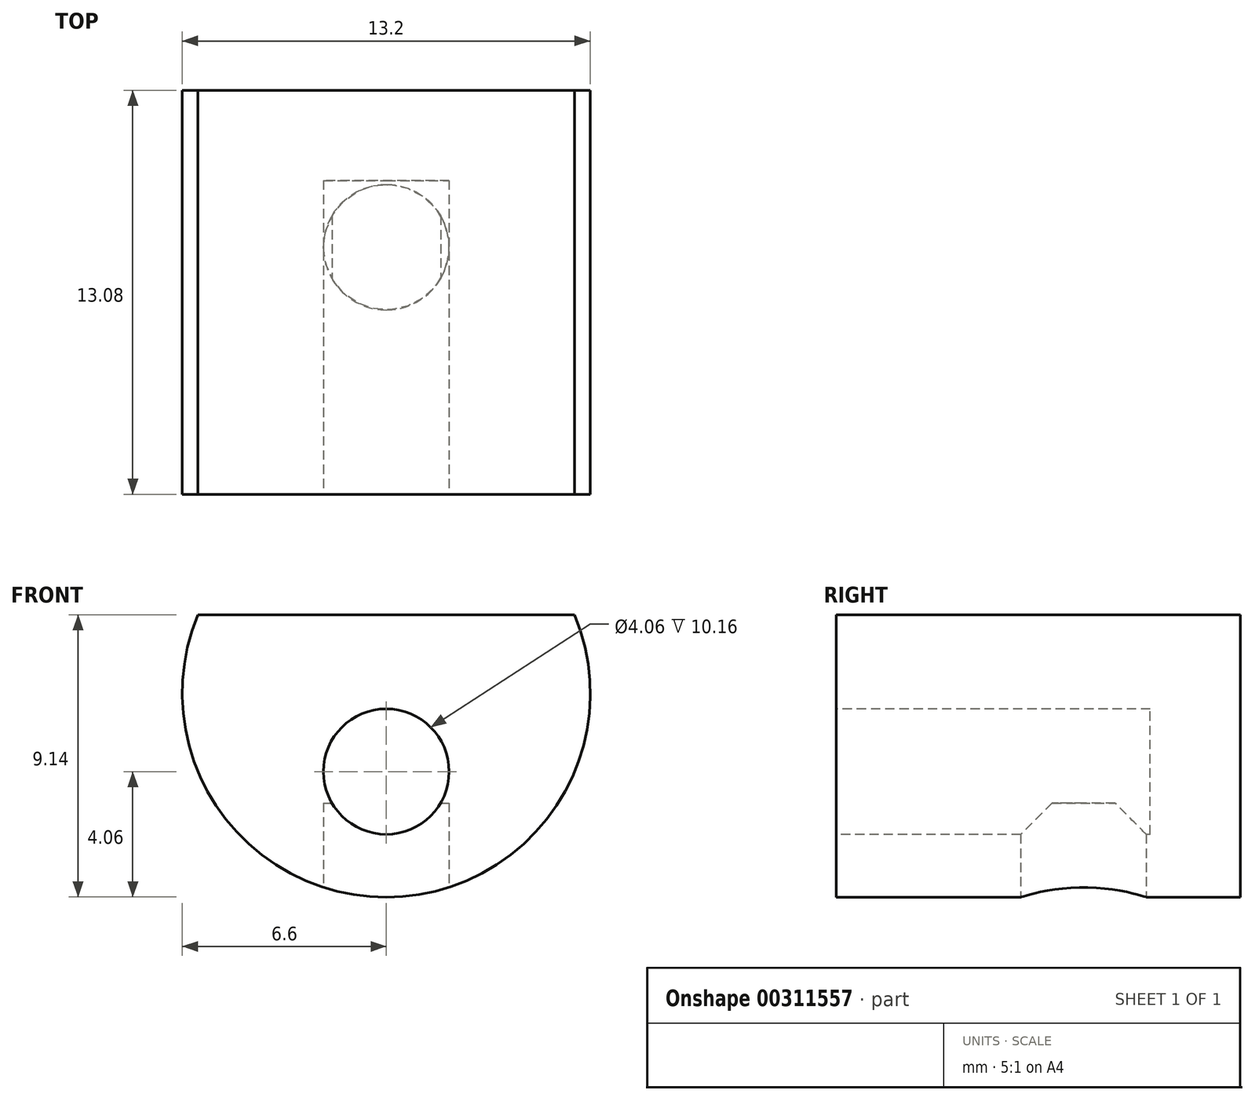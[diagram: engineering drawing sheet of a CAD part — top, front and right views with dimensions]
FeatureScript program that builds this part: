
annotation { "Feature Type Name" : "Feature", "Feature Type Description" : "" }
export const myFeature = defineFeature(function(context is Context, id is Id, definition is map)
    precondition{}
    {
        {
            var Q0;
            Q0=qCreatedBy(makeId("Front.planeOp"),FACE);
            var sketch = newSketch(context, id + "F0", { "sketchPlane" : qUnion([Q0])});
            skLineSegment(sketch, "E0", {"start": v(-6.6, 0) * mm, "end": v(6.6, 0) * mm});
            skCircle(sketch, "E1", {"center": v(0, 0) * mm, "radius": 6.6 * mm});
            skSolve(sketch);
        }
        {
            var Q0;
            {var subQ0=sQuery(id+"F0.wireOp",EDGE,"E0");Q0=makeQuery(id+"F0.imprint","IMPRINT",FACE,{"disambiguationData":[TD([[makeQuery(id+"F0.imprint","IMPRINT",EDGE,{"derivedFrom":subQ0}),1.0]])]});}
            var Q1;
            {var subQ0=sQuery(id+"F0.wireOp",EDGE,"E0");Q1=makeQuery(id+"F0.imprint","IMPRINT",FACE,{"disambiguationData":[TD([[makeQuery(id+"F0.imprint","IMPRINT",EDGE,{"derivedFrom":subQ0}),-1.0]])]});}
            extrude(context, id + "F1", {"entities" : qUnion([Q0, Q1]), "depth" : 13.08 * mm});
        }
        {
            var Q0;
            Q0=makeQuery(id+"F1.opExtrude","CAP_FACE",FACE,{"disambiguationData":[OSD([sQuery(id+"F0.wireOp",EDGE,"E1")])],"isStart":false});
            var sketch = newSketch(context, id + "F2", { "sketchPlane" : qUnion([Q0])});
            skPoint(sketch, "E2", {"position": v(0, -2.54) * mm});
            skCircle(sketch, "E3", {"center": v(0, -2.54) * mm, "radius": 2.03 * mm});
            skSolve(sketch);
        }
        {
            var Q0;
            Q0=makeQuery(id+"F2.imprint","IMPRINT",FACE,{"disambiguationData":[TD([[makeQuery(id+"F2.imprint","IMPRINT",EDGE,{"derivedFrom":sQuery(id+"F2.wireOp",EDGE,"E3")}),1.0]])]});
            extrude(context, id + "F3", {"entities" : qUnion([Q0]), "operationType" : NewBodyOperationType.REMOVE, "oppositeDirection" : true, "depth" : 10.16 * mm});
        }
        {
            var Q0;
            Q0=makeQuery(id+"F1.opExtrude","CAP_FACE",FACE,{"disambiguationData":[OSD([sQuery(id+"F0.wireOp",EDGE,"E1")])],"isStart":false});
            var sketch = newSketch(context, id + "F4", { "sketchPlane" : qUnion([Q0])});
            skPoint(sketch, "E4", {"position": v(0, 2.54) * mm});
            skLineSegment(sketch, "E5", {"start": v(-6.1, 2.54) * mm, "end": v(6.1, 2.54) * mm});
            skSolve(sketch);
        }
        {
            var Q0;
            {var subQ0=sQuery(id+"F4.wireOp",EDGE,"E5");Q0=makeQuery(id+"F4.imprint","IMPRINT",FACE,{"disambiguationData":[TD([[makeQuery(id+"F4.imprint","IMPRINT",EDGE,{"derivedFrom":subQ0}),1.0]])]});}
            extrude(context, id + "F5", {"entities" : qUnion([Q0]), "operationType" : NewBodyOperationType.REMOVE, "endBound" : BoundingType.THROUGH_ALL, "oppositeDirection" : true, "depth" : 25.4 * mm});
        }
        {
            var Q0;
            Q0=qCreatedBy(makeId("Top.planeOp"),FACE);
            cPlane(context, id + "F6", {"entities" : qUnion([Q0]), "cplaneType" : CPlaneType.OFFSET, "offset" : 6.6 * mm, "oppositeDirection" : true, "width" : 152.4 * mm, "height" : 152.4 * mm});
        }
        {
            var Q0;
            Q0=qCreatedBy(id+"F6.planeOp",FACE);
            var sketch = newSketch(context, id + "F7", { "sketchPlane" : qUnion([Q0])});
            skPoint(sketch, "E6", {"position": v(0, -5.08) * mm});
            skCircle(sketch, "E7", {"center": v(0, -5.08) * mm, "radius": 2.03 * mm});
            skSolve(sketch);
        }
        {
            var Q0;
            Q0=makeQuery(id+"F7.imprint","IMPRINT",FACE,{"disambiguationData":[TD([[makeQuery(id+"F7.imprint","IMPRINT",EDGE,{"derivedFrom":sQuery(id+"F7.wireOp",EDGE,"E7")}),1.0]])]});
            extrude(context, id + "F8", {"entities" : qUnion([Q0]), "operationType" : NewBodyOperationType.REMOVE, "depth" : 3.05 * mm});
        }
    });
